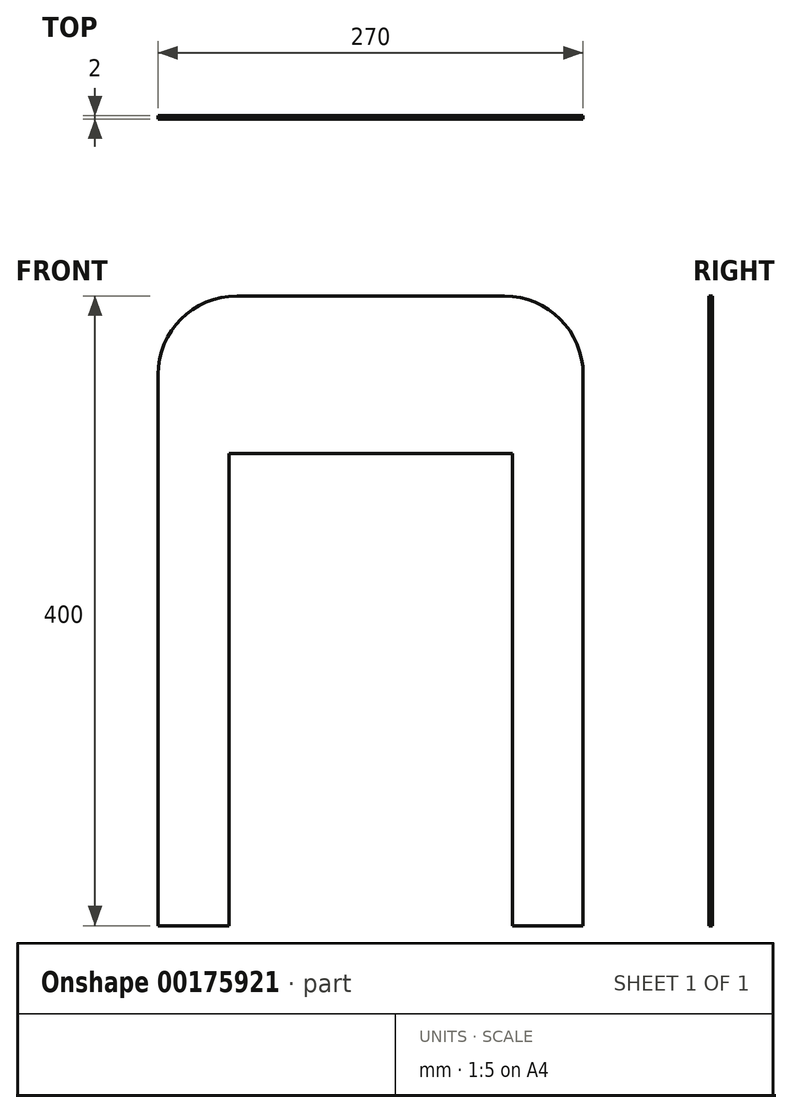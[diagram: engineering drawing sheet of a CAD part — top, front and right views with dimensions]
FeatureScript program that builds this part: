
annotation { "Feature Type Name" : "Feature", "Feature Type Description" : "" }
export const myFeature = defineFeature(function(context is Context, id is Id, definition is map)
    precondition{}
    {
        {
            var Q0;
            Q0=qCreatedBy(makeId("Front.planeOp"),FACE);
            var sketch = newSketch(context, id + "F0", { "sketchPlane" : qUnion([Q0])});
            skLineSegment(sketch, "E0", {"start": v(0, 0) * mm, "end": v(-85, 0) * mm});
            skLineSegment(sketch, "E1", {"start": v(-135, -50) * mm, "end": v(-135, -400) * mm});
            skLineSegment(sketch, "E2", {"start": v(-135, -400) * mm, "end": v(-90, -400) * mm});
            skLineSegment(sketch, "E3", {"start": v(-90, -400) * mm, "end": v(-90, -100) * mm});
            skLineSegment(sketch, "E4", {"start": v(-90, -100) * mm, "end": v(0, -100) * mm});
            skLineSegment(sketch, "E5.MirrorCS", {"start": v(135, -400) * mm, "end": v(90, -400) * mm});
            skLineSegment(sketch, "E6.MirrorCS", {"start": v(0, 0) * mm, "end": v(85, 0) * mm});
            skLineSegment(sketch, "E7.MirrorCS", {"start": v(90, -100) * mm, "end": v(0, -100) * mm});
            skLineSegment(sketch, "E8.MirrorCS", {"start": v(135, -50) * mm, "end": v(135, -400) * mm});
            skLineSegment(sketch, "E9.MirrorCS", {"start": v(90, -400) * mm, "end": v(90, -100) * mm});
            skPoint(sketch, "E10.visualSharp", {"position": v(-135, 0) * mm});
            skArc(sketch, "E10.filletArc", {"start": v(-85, 0) * mm, "mid": v(-120.36, -14.64) * mm, "end": v(-135, -50) * mm});
            skPoint(sketch, "E11.visualSharp", {"position": v(135, 0) * mm});
            skArc(sketch, "E11.filletArc", {"start": v(135, -50) * mm, "mid": v(120.36, -14.64) * mm, "end": v(85, 0) * mm});
            skSolve(sketch);
        }
        {
            var Q0;
            Q0=makeQuery(id+"F0.imprint","IMPRINT",FACE,{"disambiguationData":[TD([[makeQuery(id+"F0.imprint","IMPRINT",EDGE,{"derivedFrom":sQuery(id+"F0.wireOp",EDGE,"E0")}),1.0]])]});
            extrude(context, id + "F1", {"entities" : qUnion([Q0]), "depth" : 2 * mm});
        }
    });
